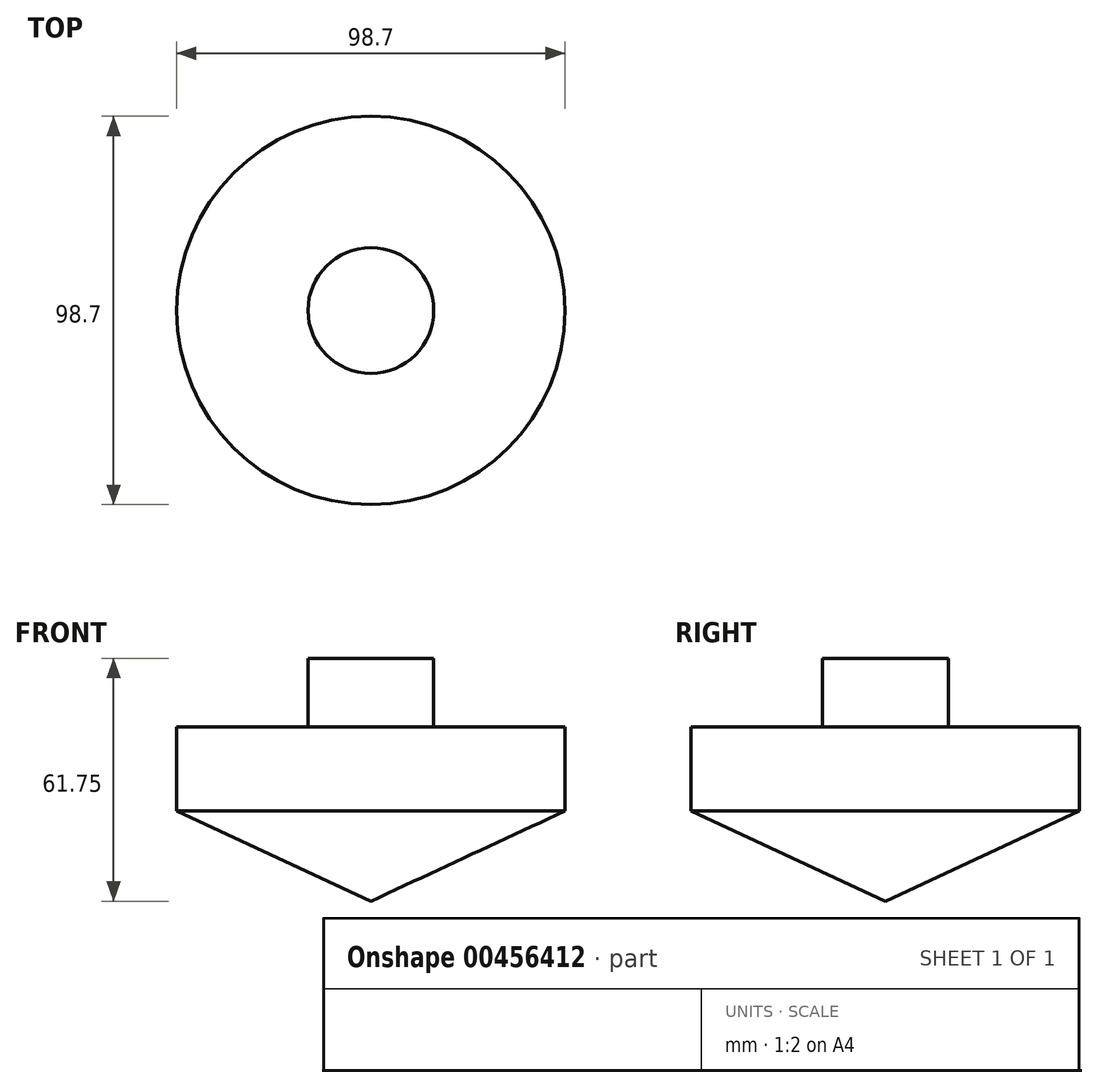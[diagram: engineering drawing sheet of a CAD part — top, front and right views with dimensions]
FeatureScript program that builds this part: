
annotation { "Feature Type Name" : "Feature", "Feature Type Description" : "" }
export const myFeature = defineFeature(function(context is Context, id is Id, definition is map)
    precondition{}
    {
        {
            var Q0;
            Q0=qCreatedBy(makeId("Front.planeOp"),FACE);
            var sketch = newSketch(context, id + "F0", { "sketchPlane" : qUnion([Q0])});
            skLineSegment(sketch, "E0", {"start": v(0, 0) * mm, "end": v(49.35, 22.96) * mm});
            skLineSegment(sketch, "E1", {"start": v(49.35, 22.96) * mm, "end": v(49.35, 44.35) * mm});
            skLineSegment(sketch, "E2", {"start": v(49.35, 44.35) * mm, "end": v(15.97, 44.35) * mm});
            skLineSegment(sketch, "E3", {"start": v(15.97, 44.35) * mm, "end": v(15.97, 61.75) * mm});
            skLineSegment(sketch, "E4", {"start": v(15.97, 61.75) * mm, "end": v(0, 61.75) * mm});
            skLineSegment(sketch, "E5", {"start": v(0, 61.75) * mm, "end": v(0, 0) * mm});
            skSolve(sketch);
        }
        {
            var Q0;
            Q0=qSketchRegion(id+"F0",true);
            var Q1;
            Q1=sQuery(id+"F0.wireOp",EDGE,"E5");
            revolve(context, id + "F1", {"entities" : qUnion([Q0]), "axis" : qUnion([Q1]), "revolveType" : RevolveType.FULL});
        }
    });
